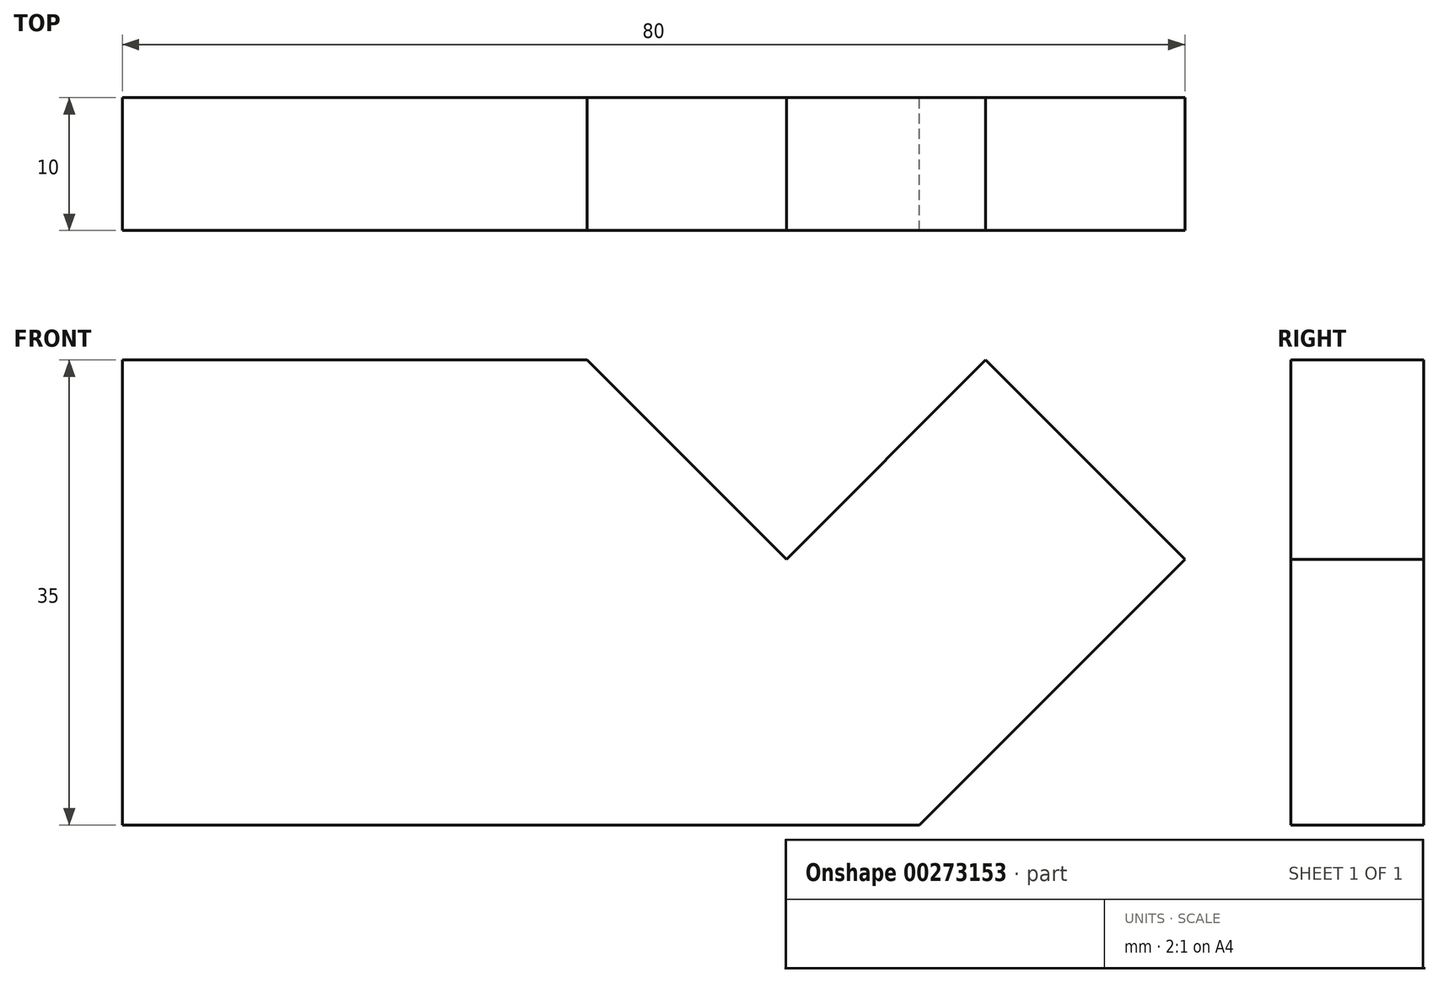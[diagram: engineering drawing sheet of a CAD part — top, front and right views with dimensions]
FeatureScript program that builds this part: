
annotation { "Feature Type Name" : "Feature", "Feature Type Description" : "" }
export const myFeature = defineFeature(function(context is Context, id is Id, definition is map)
    precondition{}
    {
        {
            var Q0;
            Q0=qCreatedBy(makeId("Front.planeOp"),FACE);
            var sketch = newSketch(context, id + "F0", { "sketchPlane" : qUnion([Q0])});
            skLineSegment(sketch, "E0", {"start": v(0, 0) * mm, "end": v(0, 35) * mm});
            skLineSegment(sketch, "E1", {"start": v(0, 35) * mm, "end": v(35, 35) * mm});
            skLineSegment(sketch, "E2", {"start": v(0, 0) * mm, "end": v(60, 0) * mm});
            skLineSegment(sketch, "E3", {"start": v(60, 0) * mm, "end": v(80, 20) * mm});
            skLineSegment(sketch, "E4", {"start": v(65, 35) * mm, "end": v(50, 20) * mm});
            skLineSegment(sketch, "E5", {"start": v(50, 20) * mm, "end": v(35, 35) * mm});
            skLineSegment(sketch, "E6", {"start": v(80, 20) * mm, "end": v(65, 35) * mm});
            skSolve(sketch);
        }
        {
            var Q0;
            Q0=makeQuery(id+"F0.imprint","IMPRINT",FACE,{"disambiguationData":[TD([[makeQuery(id+"F0.imprint","IMPRINT",EDGE,{"derivedFrom":sQuery(id+"F0.wireOp",EDGE,"E0")}),-1.0]])]});
            extrude(context, id + "F1", {"entities" : qUnion([Q0]), "depth" : 10 * mm});
        }
    });
